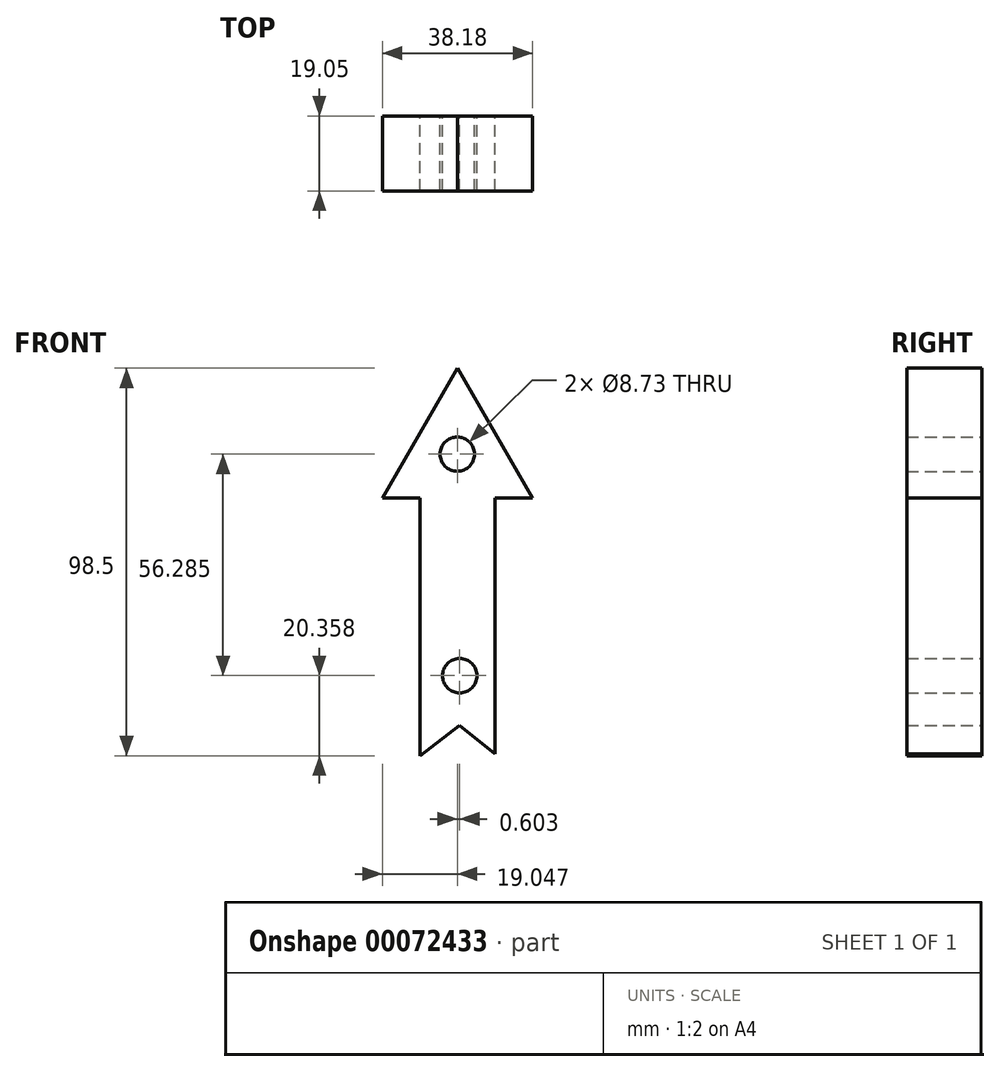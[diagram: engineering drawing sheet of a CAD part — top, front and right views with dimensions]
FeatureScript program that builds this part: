
annotation { "Feature Type Name" : "Feature", "Feature Type Description" : "" }
export const myFeature = defineFeature(function(context is Context, id is Id, definition is map)
    precondition{}
    {
        {
            var Q0;
            Q0=qCreatedBy(makeId("Front.planeOp"),FACE);
            var sketch = newSketch(context, id + "F0", { "sketchPlane" : qUnion([Q0])});
            skLineSegment(sketch, "E0.top", {"start": v(-10.13, 51.84) * mm, "end": v(8.92, 51.84) * mm});
            skLineSegment(sketch, "E0.left", {"start": v(-10.13, -24.8) * mm, "end": v(-10.13, 51.84) * mm});
            skLineSegment(sketch, "E0.right", {"start": v(8.92, -24.36) * mm, "end": v(8.92, 51.84) * mm});
            skPoint(sketch, "E1.cCircle.centerSnap0", {"position": v(-0.6, 51.84) * mm});
            skLineSegment(sketch, "E1.0", {"start": v(-19.65, 40.65) * mm, "end": v(-0.6, 73.7) * mm});
            skLineSegment(sketch, "E1.1", {"start": v(-0.6, 73.7) * mm, "end": v(18.53, 40.75) * mm});
            skLineSegment(sketch, "E1.2", {"start": v(18.53, 40.75) * mm, "end": v(-19.65, 40.65) * mm});
            skPoint(sketch, "E1.0.midPoint", {"position": v(-10.13, 57.18) * mm});
            skCircle(sketch, "E2", {"center": v(-0.6, 51.84) * mm, "radius": 4.37 * mm});
            skLineSegment(sketch, "E3", {"start": v(-10.13, -24.8) * mm, "end": v(0, -17.14) * mm});
            skLineSegment(sketch, "E4", {"start": v(0, -17.14) * mm, "end": v(8.92, -24.36) * mm});
            skCircle(sketch, "E5", {"center": v(0, -4.44) * mm, "radius": 4.37 * mm});
            skSolve(sketch);
        }
        {
            var Q0;
            Q0 = qSketchRegion(id + "F0", true);
            var Q1;
            {var subQ1=sQuery(id+"F0.wireOp",EDGE,"E0.top");var subQ8=sQuery(id+"F0.wireOp",EDGE,"E0.left");var subQ9=makeQuery(id+"F0.imprint","INTERSECT",VERTEX,{"derivedFrom":[subQ1,subQ8]});Q1=makeQuery(id+"F0.imprint","IMPRINT",FACE,{"disambiguationData":[TD([[makeQuery(id+"F0.imprint","IMPRINT",EDGE,{"disambiguationData":[TD([[subQ9,-1.0]])],"derivedFrom":subQ1}),-1.0]])]});}
            extrude(context, id + "F1", {"entities" : qUnion([Q0, Q1]), "depth" : 19.05 * mm});
        }
    });
